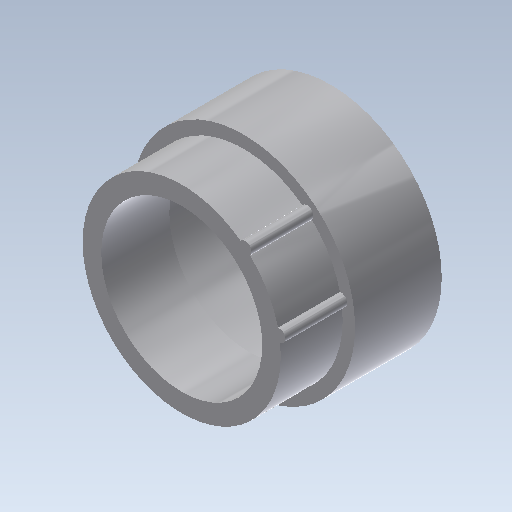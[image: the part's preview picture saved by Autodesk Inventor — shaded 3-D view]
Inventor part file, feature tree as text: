
AUTODESK INVENTOR PART (.ipt)
format: ipt  version: 2020 (Build 240168000, 168)  size: 160,768 bytes
history: native  units: mm
features: sketch x2, revolve x1, extrude x1
ambient origin geometry x8: Origin, YZ Plane, XZ Plane, XY Plane, X Axis, Y Axis, Z Axis, Center Point
bodies: Body1 (feature_tree)
feature tree (4):
  revolve  "Revolution1"  [1 undecoded]
  extrude  "Extrusion4"  TaperAngle=0.0deg  [1 undecoded]
  sketch  "Sketch4"  dims[d9=18.0mm d10=16.0mm]
  sketch  "Sketch5"  dims[d13=7.0mm d14=0.0mm d15=5.0mm d16=6.5mm d17=13.0mm d18=16.0mm d19=90.0deg d20=1.745329mm d21=6.981317mm d22=1.0mm d23=1.0mm d24=5.0mm d25=0.0mm]
note: 2 required parameter values undecoded (feature->parameter linkage not recoverable at this tier; creation-order binding heuristic only, values carry confidence <= 0.55)